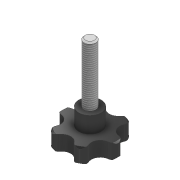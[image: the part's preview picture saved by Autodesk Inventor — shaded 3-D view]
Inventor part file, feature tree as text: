
AUTODESK INVENTOR PART (.ipt)
format: ipt  version: 2020 (Build 240168000, 168)  size: 183,808 bytes
history: native  units: mm
features: extrude x4, sketch x4, chamfer x2, thread x1, pattern_circular x1, fillet x1
ambient origin geometry x8: Origin, YZ Plane, XZ Plane, XY Plane, X Axis, Y Axis, Z Axis, Center Point
bodies: Solid1 (feature_tree)
feature tree (13):
  extrude  "Extrusion1"  Depth=10.0mm TaperAngle=0.0deg
  extrude  "Extrusion2"  Depth=11.0mm TaperAngle=0.0deg
  extrude  "Extrusion3"  Depth=40.0mm TaperAngle=0.0deg
  thread  "Thread1"  [1 undecoded]
  chamfer  "Chamfer1"  Distance=1.0mm Angle=45.0deg
  chamfer  "Chamfer2"  Distance=1.0mm Angle=45.0deg
  extrude  "Extrusion4"  Depth=3.5mm TaperAngle=0.0deg
  pattern_circular  "Circular Pattern1"  Count=6 Angle=360.0deg
  fillet  "Fillet1"  Radius=3.5mm
  sketch  "Sketch1"  dims[d0=38.0mm d1=10.0mm d2=0.0mm]
  sketch  "Sketch2"  dims[d3=15.0mm d4=11.0mm d5=0.0mm]
  sketch  "Sketch3"  dims[d6=8.0mm d7=40.0mm d8=0.0mm d9=180.0mm d10=0.0mm d11=1.0mm d12=2.0mm d13=45.0deg d14=1.0mm d15=2.0mm d16=45.0deg]
  sketch  "Sketch4"  dims[d17=12.0mm d18=40.0mm d19=0.0mm d20=60.0mm d21=360.0deg d23=3.5mm]
note: 1 required parameter value undecoded (feature->parameter linkage not recoverable at this tier; creation-order binding heuristic only, values carry confidence <= 0.55)
